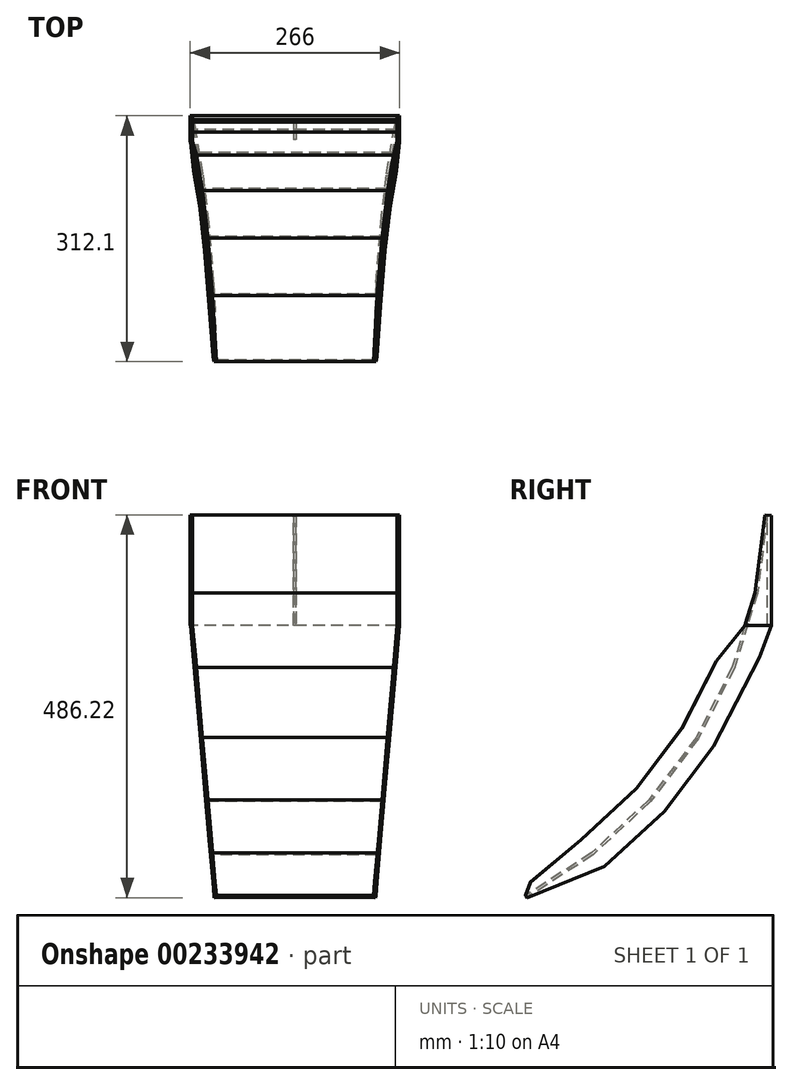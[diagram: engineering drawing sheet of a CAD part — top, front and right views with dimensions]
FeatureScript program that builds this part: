
annotation { "Feature Type Name" : "Feature", "Feature Type Description" : "" }
export const myFeature = defineFeature(function(context is Context, id is Id, definition is map)
    precondition{}
    {
        {
            var Q0;
            Q0=qCreatedBy(makeId("Front.planeOp"),FACE);
            var sketch = newSketch(context, id + "F0", { "sketchPlane" : qUnion([Q0])});
            skLineSegment(sketch, "E0.bottom", {"start": v(130, -70) * mm, "end": v(-130, -70) * mm});
            skLineSegment(sketch, "E0.top", {"start": v(130, 70) * mm, "end": v(-130, 70) * mm});
            skLineSegment(sketch, "E0.left", {"start": v(130, -70) * mm, "end": v(130, 70) * mm});
            skLineSegment(sketch, "E0.right", {"start": v(-130, -70) * mm, "end": v(-130, 70) * mm});
            skPoint(sketch, "E0.middle", {"position": v(0, 0) * mm});
            skSolve(sketch);
        }
        {
            var Q0;
            Q0 = qSketchRegion(id + "F0", true);
            extrude(context, id + "F1", {"entities" : qUnion([Q0]), "depth" : 5 * mm});
        }
        {
            var Q0;
            Q0=qCreatedBy(makeId("Right.planeOp"),FACE);
            var sketch = newSketch(context, id + "F2", { "sketchPlane" : qUnion([Q0])});
            skLineSegment(sketch, "E1.0", {"start": v(-5, -70) * mm, "end": v(-5, 70) * mm, "construction": true});
            skLineSegment(sketch, "E2", {"start": v(-5, 70) * mm, "end": v(-17.49, -29.22) * mm});
            skLineSegment(sketch, "E3", {"start": v(-17.49, -29.22) * mm, "end": v(-47.01, -124.76) * mm});
            skLineSegment(sketch, "E4", {"start": v(-47.01, -124.76) * mm, "end": v(-92.68, -213.72) * mm});
            skLineSegment(sketch, "E5", {"start": v(-92.68, -213.72) * mm, "end": v(-153.1, -293.4) * mm});
            skLineSegment(sketch, "E6", {"start": v(-153.1, -293.4) * mm, "end": v(-226.45, -361.38) * mm});
            skLineSegment(sketch, "E7", {"start": v(-404.04, -470) * mm, "end": v(295.5, -470) * mm, "construction": true});
            skLineSegment(sketch, "E8", {"start": v(-226.45, -361.38) * mm, "end": v(-310.48, -415.6) * mm});
            skLineSegment(sketch, "E9.0", {"start": v(-228.3, -359) * mm, "end": v(-312.1, -413.07) * mm});
            skLineSegment(sketch, "E9.1", {"start": v(-155.34, -291.38) * mm, "end": v(-228.3, -359) * mm});
            skLineSegment(sketch, "E9.2", {"start": v(-7.98, 70.37) * mm, "end": v(-20.43, -28.58) * mm});
            skLineSegment(sketch, "E9.3", {"start": v(-20.43, -28.58) * mm, "end": v(-49.8, -123.62) * mm});
            skLineSegment(sketch, "E9.4", {"start": v(-49.8, -123.62) * mm, "end": v(-95.23, -212.12) * mm});
            skLineSegment(sketch, "E9.5", {"start": v(-95.23, -212.12) * mm, "end": v(-155.34, -291.38) * mm});
            skLineSegment(sketch, "E10", {"start": v(-310.48, -415.6) * mm, "end": v(-312.1, -413.07) * mm});
            skLineSegment(sketch, "E11", {"start": v(-7.98, 70.37) * mm, "end": v(-5, 70) * mm});
            skSolve(sketch);
        }
        {
            var Q0;
            Q0 = qSketchRegion(id + "F2", true);
            extrude(context, id + "F3", {"entities" : qUnion([Q0]), "endBound" : BoundingType.SYMMETRIC, "depth" : 260 * mm});
        }
        {
            var Q0;
            Q0=makeQuery(id+"F1.opExtrude","SWEPT_EDGE",EDGE,{"disambiguationData":[OSD([sQuery(id+"F0.wireOp",EDGE,"E0.bottom"),sQuery(id+"F0.wireOp",EDGE,"E0.left")])]});
            cPoint(context, id + "F4", {"entities" : qUnion([Q0]), "parameter" : 0.5});
        }
        {
            var Q0;
            Q0=makeQuery(id+"F1.opExtrude","SWEPT_EDGE",EDGE,{"disambiguationData":[OSD([sQuery(id+"F0.wireOp",EDGE,"E0.top"),sQuery(id+"F0.wireOp",EDGE,"E0.left")])]});
            var Q1;
            Q1 = qCreatedBy(id + "F4" ,VERTEX);
            cPlane(context, id + "F5", {"entities" : qUnion([Q0, Q1]), "cplaneType" : CPlaneType.LINE_ANGLE, "offset" : 25 * mm, "angle" : 5 * degree, "width" : 150 * mm, "height" : 150 * mm});
        }
        {
            var Q0;
            Q0=qCreatedBy(id+"F5.planeOp",FACE);
            cPlane(context, id + "F6", {"entities" : qUnion([Q0]), "cplaneType" : CPlaneType.OFFSET, "offset" : 12 * mm, "oppositeDirection" : true, "width" : 150 * mm, "height" : 150 * mm});
        }
        {
            var Q0;
            Q0=qCreatedBy(id+"F6.planeOp",FACE);
            var sketch = newSketch(context, id + "F7", { "sketchPlane" : qUnion([Q0])});
            skLineSegment(sketch, "E12.bottom", {"start": v(478.7, 168.79) * mm, "end": v(-178.55, 168.79) * mm});
            skLineSegment(sketch, "E12.top", {"start": v(478.7, -464.12) * mm, "end": v(-178.55, -464.12) * mm});
            skLineSegment(sketch, "E12.left", {"start": v(478.7, 168.79) * mm, "end": v(478.7, -464.12) * mm});
            skLineSegment(sketch, "E12.right", {"start": v(-178.55, 168.79) * mm, "end": v(-178.55, -464.12) * mm});
            skSolve(sketch);
        }
        {
            var Q0;
            Q0 = qSketchRegion(id + "F7", true);
            extrude(context, id + "F8", {"entities" : qUnion([Q0]), "oppositeDirection" : true, "depth" : 174 * mm});
        }
        {
            var Q0;
            Q0=makeQuery(id+"F8.opExtrude","SWEPT_BODY",BODY,{"disambiguationData":[OSD([sQuery(id+"F7.wireOp",EDGE,"E12.bottom"),sQuery(id+"F7.wireOp",EDGE,"E12.top"),sQuery(id+"F7.wireOp",EDGE,"E12.left"),sQuery(id+"F7.wireOp",EDGE,"E12.right")])]});
            var Q1;
            Q1=qCreatedBy(makeId("Right.planeOp"),FACE);
            mirror(context, id + "F9", {"entities" : qUnion([Q0]), "mirrorPlane" : qUnion([Q1])});
        }
        {
            var Q0;
            Q0=makeQuery(id+"F9.opPattern","COPY",BODY,{"derivedFrom":makeQuery(id+"F8.opExtrude","SWEPT_BODY",BODY,{"disambiguationData":[OSD([sQuery(id+"F7.wireOp",EDGE,"E12.bottom"),sQuery(id+"F7.wireOp",EDGE,"E12.top"),sQuery(id+"F7.wireOp",EDGE,"E12.left"),sQuery(id+"F7.wireOp",EDGE,"E12.right")])]}),"instanceName":"1"});
            var Q1;
            Q1=makeQuery(id+"F8.opExtrude","SWEPT_BODY",BODY,{"disambiguationData":[OSD([sQuery(id+"F7.wireOp",EDGE,"E12.bottom"),sQuery(id+"F7.wireOp",EDGE,"E12.top"),sQuery(id+"F7.wireOp",EDGE,"E12.left"),sQuery(id+"F7.wireOp",EDGE,"E12.right")])]});
            var Q2;
            Q2=makeQuery(id+"F3.opExtrude","SWEPT_BODY",BODY,{"disambiguationData":[OSD([sQuery(id+"F2.wireOp",EDGE,"E2"),sQuery(id+"F2.wireOp",EDGE,"E3"),sQuery(id+"F2.wireOp",EDGE,"E4"),sQuery(id+"F2.wireOp",EDGE,"E5"),sQuery(id+"F2.wireOp",EDGE,"E6"),sQuery(id+"F2.wireOp",EDGE,"E8"),sQuery(id+"F2.wireOp",EDGE,"E9.0"),sQuery(id+"F2.wireOp",EDGE,"E9.1"),sQuery(id+"F2.wireOp",EDGE,"E9.2"),sQuery(id+"F2.wireOp",EDGE,"E9.3"),sQuery(id+"F2.wireOp",EDGE,"E9.4"),sQuery(id+"F2.wireOp",EDGE,"E9.5"),sQuery(id+"F2.wireOp",EDGE,"E10"),sQuery(id+"F2.wireOp",EDGE,"E11")])]});
            booleanBodies(context, id + "F10", {"operationType" : BooleanOperationType.SUBTRACTION, "tools" : qUnion([Q0, Q1]), "targets" : qUnion([Q2])});
        }
        {
            var Q0;
            Q0=qCreatedBy(id+"F6.planeOp",FACE);
            var sketch = newSketch(context, id + "F11", { "sketchPlane" : qUnion([Q0])});
            skLineSegment(sketch, "E13.2", {"start": v(241.81, -331.62) * mm, "end": v(171.42, -266.12) * mm});
            skLineSegment(sketch, "E13.3", {"start": v(171.42, -266.12) * mm, "end": v(113.42, -189.35) * mm});
            skLineSegment(sketch, "E13.4", {"start": v(113.42, -189.35) * mm, "end": v(69.58, -103.62) * mm});
            skLineSegment(sketch, "E14.2", {"start": v(211.57, -365.68) * mm, "end": v(135.67, -295.05) * mm});
            skLineSegment(sketch, "E14.3", {"start": v(135.67, -295.05) * mm, "end": v(73.14, -212.28) * mm});
            skLineSegment(sketch, "E14.4", {"start": v(73.14, -212.28) * mm, "end": v(15.17, -98.92) * mm});
            skLineSegment(sketch, "E15", {"start": v(15.17, -98.92) * mm, "end": v(0, -58.4) * mm});
            skLineSegment(sketch, "E16", {"start": v(211.57, -365.68) * mm, "end": v(310.48, -405.33) * mm});
            skLineSegment(sketch, "E17", {"start": v(310.48, -405.33) * mm, "end": v(312.1, -402.8) * mm});
            skLineSegment(sketch, "E18", {"start": v(312.1, -402.8) * mm, "end": v(305.65, -385.56) * mm});
            skLineSegment(sketch, "E19", {"start": v(305.65, -385.56) * mm, "end": v(241.81, -331.62) * mm});
            skLineSegment(sketch, "E20", {"start": v(0, -58.4) * mm, "end": v(33.23, -58.4) * mm});
            skLineSegment(sketch, "E21", {"start": v(33.23, -58.4) * mm, "end": v(69.58, -103.62) * mm});
            skSolve(sketch);
        }
        {
            var Q0;
            Q0 = qSketchRegion(id + "F11", true);
            extrude(context, id + "F12", {"entities" : qUnion([Q0]), "oppositeDirection" : true, "depth" : 3 * mm});
        }
        {
            var Q0;
            Q0=makeQuery(id+"F1.opExtrude","SWEPT_FACE",FACE,{"disambiguationData":[OSD([sQuery(id+"F0.wireOp",EDGE,"E0.left")])]});
            var sketch = newSketch(context, id + "F13", { "sketchPlane" : qUnion([Q0])});
            skLineSegment(sketch, "E22", {"start": v(-7.98, 70.37) * mm, "end": v(0, 70) * mm});
            skLineSegment(sketch, "E23", {"start": v(0, 70) * mm, "end": v(0, -70) * mm});
            skLineSegment(sketch, "E24", {"start": v(0, -70) * mm, "end": v(-33.23, -70) * mm});
            skPoint(sketch, "E24.endSnap0", {"position": v(-2.5, -70) * mm});
            skLineSegment(sketch, "E25", {"start": v(-33.23, -70) * mm, "end": v(-20.43, -28.58) * mm});
            skLineSegment(sketch, "E26", {"start": v(-20.43, -28.58) * mm, "end": v(-7.98, 70.37) * mm});
            skSolve(sketch);
        }
        {
            var Q0;
            Q0 = qSketchRegion(id + "F13", true);
            extrude(context, id + "F14", {"entities" : qUnion([Q0]), "depth" : 3 * mm});
        }
        {
            var Q0;
            Q0=qCreatedBy(makeId("Right.planeOp"),FACE);
            var sketch = newSketch(context, id + "F15", { "sketchPlane" : qUnion([Q0])});
            skLineSegment(sketch, "E27.0", {"start": v(-5, -70) * mm, "end": v(-5, 70) * mm});
            skLineSegment(sketch, "E28.0", {"start": v(-5, 70) * mm, "end": v(-17.49, -29.22) * mm});
            skLineSegment(sketch, "E29.0", {"start": v(-17.49, -29.22) * mm, "end": v(-29.38, -67.68) * mm});
            skLineSegment(sketch, "E30", {"start": v(-5, -70) * mm, "end": v(-30.1, -70) * mm});
            skLineSegment(sketch, "E31", {"start": v(-30.1, -70) * mm, "end": v(-29.38, -67.68) * mm});
            skSolve(sketch);
        }
        {
            var Q0;
            Q0 = qSketchRegion(id + "F15", true);
            extrude(context, id + "F16", {"entities" : qUnion([Q0]), "endBound" : BoundingType.SYMMETRIC, "depth" : 3 * mm});
        }
        {
            var Q0;
            Q0=makeQuery(id+"F14.opExtrude","SWEPT_BODY",BODY,{"disambiguationData":[OSD([sQuery(id+"F13.wireOp",EDGE,"E22"),sQuery(id+"F13.wireOp",EDGE,"E23"),sQuery(id+"F13.wireOp",EDGE,"E24"),sQuery(id+"F13.wireOp",EDGE,"E25"),sQuery(id+"F13.wireOp",EDGE,"E26")])]});
            var Q1;
            Q1=makeQuery(id+"F12.opExtrude","SWEPT_BODY",BODY,{"disambiguationData":[OSD([sQuery(id+"F11.wireOp",EDGE,"E13.2"),sQuery(id+"F11.wireOp",EDGE,"E13.3"),sQuery(id+"F11.wireOp",EDGE,"E13.4"),sQuery(id+"F11.wireOp",EDGE,"E14.2"),sQuery(id+"F11.wireOp",EDGE,"E14.3"),sQuery(id+"F11.wireOp",EDGE,"E14.4"),sQuery(id+"F11.wireOp",EDGE,"E15"),sQuery(id+"F11.wireOp",EDGE,"E16"),sQuery(id+"F11.wireOp",EDGE,"E17"),sQuery(id+"F11.wireOp",EDGE,"E18"),sQuery(id+"F11.wireOp",EDGE,"E19"),sQuery(id+"F11.wireOp",EDGE,"E20"),sQuery(id+"F11.wireOp",EDGE,"E21")])]});
            var Q2;
            Q2=qCreatedBy(makeId("Right.planeOp"),FACE);
            mirror(context, id + "F17", {"entities" : qUnion([Q0, Q1]), "mirrorPlane" : qUnion([Q2])});
        }
    });
